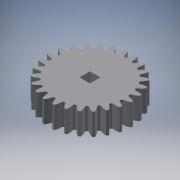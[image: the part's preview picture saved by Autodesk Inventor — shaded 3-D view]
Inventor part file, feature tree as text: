
AUTODESK INVENTOR PART (.ipt)
format: ipt  version: 2017 (Build 210142000, 142)  size: 224,768 bytes
history: native  units: mm
features: extrude x3, sketch x2, pattern_circular x1
ambient origin geometry x8: Origin, YZ Plane, XZ Plane, XY Plane, X Axis, Y Axis, Z Axis, Center Point
bodies: Solid1 (feature_tree)
feature tree (6):
  sketch  "Sketch1"  dims[d0=20.0mm d1=0.0mm]
  extrude  "Extrusion1"  TaperAngle=0.0deg  [1 undecoded]
  extrude  "Extrusion2"  Depth=9.525mm TaperAngle=360.0deg
  pattern_circular  "Circular Pattern1"  [2 undecoded]
  extrude  "Extrusion3"  Depth=9.525mm TaperAngle=0.0deg
  sketch  "Sketch2"  dims[d2=10.0mm d3=0.0mm d4=260.0mm d5=360.0deg d7=9.525mm d8=10.0mm d9=0.0mm]
note: 3 required parameter values undecoded (feature->parameter linkage not recoverable at this tier; creation-order binding heuristic only, values carry confidence <= 0.55)
